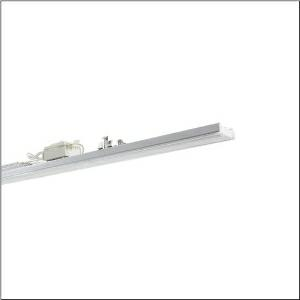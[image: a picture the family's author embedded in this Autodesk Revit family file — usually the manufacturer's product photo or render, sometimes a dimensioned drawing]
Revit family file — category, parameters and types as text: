
# Revit family: licross_11_recessed_mo_51tl12cn49xg
name_source: partatom
category: Lighting Fixtures
units: mm (PartAtom-declared; Revit-internal decimal feet)

## family parameters
Cut with Voids When Loaded = No
Host = Face
Light Source = No
Part Type = Normal
Room Calculation Point = No
Round Connector Dimension = Use Diameter
Shared = No

## types (1)
- --- (1 x LED, 9310 lm, 49.3 W, 4000K)
    Apparent Load = 49 VA
    CIE Flux Codes = 67 92 99 100 100
    Color Rendering = 80
    Color Temperature = 4000K
    Default Elevation = 1800 mm
    Description = Licross 11 Recessed MO, luminaire insert, of sheet steel, coil coated, white, length: 1.500mm, width: 66mm, height: 67mm, LED rated luminous flux: 9.310lm, light colour: 840, SDCM (Standard Deviation of Colour Matching)MacAdam ≤ 2 SDCM (initial), control gear: ON/OFF Multilumen, CLOi, with plug, 3-pole, with phase selection, mains connection: 220..240V, AC, 50/60Hz, start of lifetime: 49W, end of service life: 55W, internal wiring halogen-free, primary optical cover: cover, of PMMA, light emission: direct distribution, primary light characteristic: symmetric, protection rating (complete): IP40, insulation class (complete): insulation class I (protective earthing), certification: CE, ENEC, VDE, UKCA, protection symbol: D if used in an environment without relevant dust loads with corresponding accessories, impact resistance: IK06, permissible ambient temperature for indoor applications: -35..+40°C, corresponds to IFS (International Featured Standards) requirements for safety and quality in the food industry, reducing of maximum allowable ambient temperature of 5°C with ceiling mounting, LABS conformity tested according to VDMA 24364:2018-05, The light source and the operating device comply with the requirements of the Ecodesign Regulation (EU) 2019/2020 and are replaceable in accordance with this regulation, packaging unit: 1 piece
    Height = 58 mm
    Lamp = 1 x LED
    Lamp Light Flux = 9310 lm
    Lamp Power = 49.3 W
    Lamp count = 1
    Length = 1500 mm
    Luminous efficacy = 189 lm/W
    Manufacturer = Siteco
    ModVariant = No
    Model = 51TL12CN49XG
    Mounting Place = Ceiling
    Mounting Type = Pendant
    Number of Poles = 1
    OnlyDefault = Yes
    Power Factor = 1
    Product Name = Licross 11 Recessed MO
    Product group = luminaire insert | ceiling pendant
    ProductGroupID = 901
    Protection Class = Protection class I
    Protection Degree = IP 40
    RLX_Detail_Level = 1
    RLX_Emergency_Light_Flux = 0 lm
    RLX_Emergency_Type = 0
    RLX_Emergency_Type_DB = No
    RlxData = <blob elided: 22457 chars, md5=51a68450>
    Socket = socket
    Standby Power = 0 W
    System Light Flux = 9310 lm
    System Power = 49 W
    Type Comments = factory setting: luminous flux: 100 % | (A | C | E) | 113 mA
    Type Image = l_1296930.jpg
    URL = http://relux.com
    VarID = @adj_090899
    Voltage = 0 V
    Weight = 0.00 kg
    Width = 66 mm

## geometry (parser evidence)
native form markers: Blend x4, Sweep x11
no freeform markers — native parametric forms only
